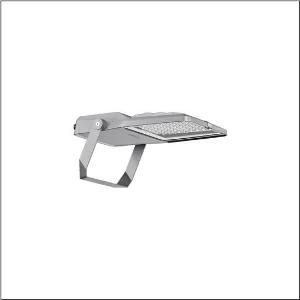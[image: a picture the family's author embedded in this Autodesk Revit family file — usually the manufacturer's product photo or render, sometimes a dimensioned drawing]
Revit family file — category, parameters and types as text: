
# Revit family: floodlight_fl_21_iq_mini___rs12_5xa7772c4b1a_5071
name_source: partatom
category: Lighting Fixtures
units: mm (PartAtom-declared; Revit-internal decimal feet)

## family parameters
Cut with Voids When Loaded = No
Host = Face
Light Source = No
Part Type = Normal
Room Calculation Point = No
Round Connector Dimension = Use Diameter
Shared = No

## types (1)
- --- (1 x LED, 12860 lm, 87.2 W, 4000K)
    Apparent Load = 87 VA
    CIE Flux Codes = 79 92 99 100 100
    Color Rendering = 70
    Color Temperature = 4000K
    Default Elevation = 1800 mm
    Description = Floodlight FL 21 iQ mini, floodlight, primary light control with lens, of PMMA, primary optical cover: protective disc, of toughened safety glass, transparent, light distribution: RS12, light emission: direct distribution, installation type: surface-mounted, lamps: LED, High Power LED, rated values: 12.860lm | 87,2W | 147,5lm/W (begin service life); end service life: 12.860lm | 92,1W; at 50% lumin. flux: 6.430lm | 40,2W | 160lm/W, colour temperature: 4000K, colour rendering: CRI > 70, light colour: 740, light setting 1 begin service life: 100% | 12.860lm | 87,2W | 147,5lm/W | 4.000K, light setting 1 end service life: 92,1W, further light settings possible, control: Street-Remote, Auto-Match, Temp-Guard, Night-Set, Smart-Wire, Desk-Remote (wireless, voltage-free reading and setting of iQ features in the workshop via application-optimized NFC function/RFID function), optimised constant luminous flux control (CLO 2.0), pre-setting: linear dimming characteristic, with terminal, 6-pole, mains connection: 220..240V, AC, 50/60Hz, luminaire housing, of diecast aluminium, powder-coated, SITECO metallic grey (DB 702S), corrosivity category C5 mid according to DIN EN ISO 12944suitable for swimming poolschlorine-resistant, sealing non-destructively replaceable, mounting bracket, of steel, galvanised, powder-coated, SITECO metallic grey (DB 702S), protection rating (complete): IP66, insulation class (complete): insulation class II (safety insulation), certification: CE, ENEC, VDE, protection symbol: D, impact resistance: IK08, permissible operating ambient temperature: -40..+40°C, permissible operating ambient temperature for outdoor applications: -40..+50°C, standard: DIN EN 12944, LABS conformity tested according to VDMA 24364:2018-05, packaging unit: 1 piece

Light Distribution: RS12
    Height = 70 mm
    Lamp = 1 x LED
    Lamp Light Flux = 12860 lm
    Lamp Power = 87.2 W
    Lamp count = 1
    Length = 485 mm
    Luminous efficacy = 147 lm/W
    Manufacturer = Siteco
    ModVariant = No
    Model = 5XA7772C4B1A
    Mounting Place = Pole
    Mounting Type = Pole annexe
    Number of Poles = 1
    OnlyDefault = Yes
    Power Factor = 1
    Product Name = Floodlight FL 21 iQ mini | RS12
    Product group = floodlight | pylon annexe
    ProductGroupID = 6201
    Protection Class = Protection class II
    Protection Degree = IP 66
    RLX_Detail_Level = 1
    RLX_Emergency_Light_Flux = 0 lm
    RLX_Emergency_Type = 0
    RLX_Emergency_Type_DB = No
    RlxData = <blob elided: 91369 chars, md5=047a8a4f>
    Socket = socket
    Standby Power = 0 W
    System Light Flux = 12860 lm
    System Power = 87 W
    Type Comments = factory setting: luminous flux: 100 % | dim-lin: 254 | 456 mA
    Type Image = l_1006845.jpg
    URL = http://relux.com
    VarID = @adj_168597
    Voltage = 0 V
    Weight = 0.00 kg
    Width = 337 mm

## geometry (parser evidence)
native form markers: Blend x4, Sweep x14
no freeform markers — native parametric forms only
